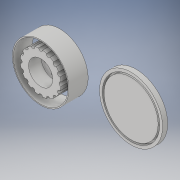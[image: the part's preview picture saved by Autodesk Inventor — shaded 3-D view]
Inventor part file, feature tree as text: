
AUTODESK INVENTOR PART (.ipt)
format: ipt  version: 2017 SP1 (Build 210196100, 196)  size: 245,248 bytes
history: native  units: in
note: dims shown in document units (in); Inventor stores cm internally (conversion verified against a paired STEP export)
features: extrude x6, sketch x6
ambient origin geometry x8: Origin, YZ Plane, XZ Plane, XY Plane, X Axis, Y Axis, Z Axis, Center Point
bodies: Solid1 (feature_tree)
feature tree (12):
  extrude  "Hub Mount"  Depth=0.1122in
  extrude  "Tire Mount"  Depth=0.1122in
  extrude  "Tire Grip Extrusion"  Depth=0.1575in
  extrude  "Tire Mold Shell"  Depth=0.25in
  extrude  "Tire Mold Base"  Depth=0.25in
  extrude  "Inset into base for shell"  Depth=0.0984in
  sketch  "Sketch1"  dims[d0=0.748in d1=0.1122in]
  sketch  "Sketch2"  dims[d2=0.1122in d3=0.1122in]
  sketch  "Sketch4"  dims[d4=0.1122in d5=0.1575in]
  sketch  "Sketch5"  dims[d6=0.25in d7=0.25in]
  sketch  "Sketch6"  dims[d8=0.25in d9=0.25in]
  sketch  "Sketch7"  dims[d10=0.1969in d11=0.0in d12=0.748in d13=1.2598in d14=0.5906in d15=0.0in d21=0.1181in d22=0.1181in d23=0.1181in d24=0.1181in d29=0.1181in d30=22.5deg d31=22.5deg d32=22.5deg d33=22.5deg d34=22.5deg d35=22.5deg d36=22.5deg d37=22.5deg d38=22.5deg d39=22.5deg d40=22.5deg d41=22.5deg d42=0.1181in d43=0.1181in d44=0.1181in d45=0.1181in d46=0.1181in d47=0.1181in d48=0.1181in d49=0.1181in d50=0.1181in d51=0.1181in d52=0.1181in d53=0.5906in d54=0.0in d55=1.6929in d56=1.752in d57=0.3937in d58=0.0in d59=1.9488in d60=2.3622in d63=0.1575in d64=0.0in d65=1.6732in d66=1.7717in d67=2.3622in d68=0.0984in d69=0.0in]
